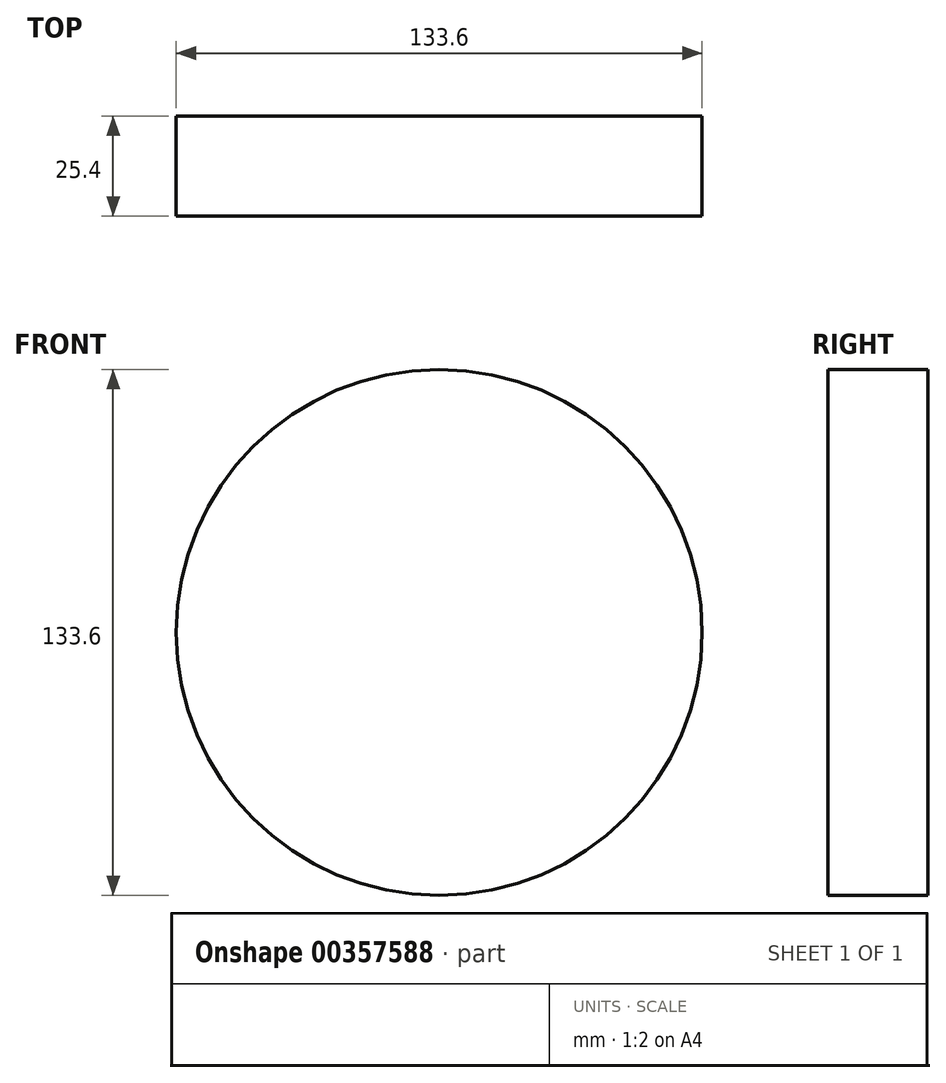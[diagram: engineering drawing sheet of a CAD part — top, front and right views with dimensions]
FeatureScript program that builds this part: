
annotation { "Feature Type Name" : "Feature", "Feature Type Description" : "" }
export const myFeature = defineFeature(function(context is Context, id is Id, definition is map)
    precondition{}
    {
        {
            var Q0;
            Q0=qCreatedBy(makeId("Front.planeOp"),FACE);
            var sketch = newSketch(context, id + "F0", { "sketchPlane" : qUnion([Q0])});
            skCircle(sketch, "E0", {"center": v(0, 0) * mm, "radius": 66.8 * mm});
            skSolve(sketch);
        }
        {
            var Q0;
            Q0 = qSketchRegion(id + "F0", true);
            extrude(context, id + "F1", {"entities" : qUnion([Q0]), "depth" : 25.4 * mm});
        }
    });
